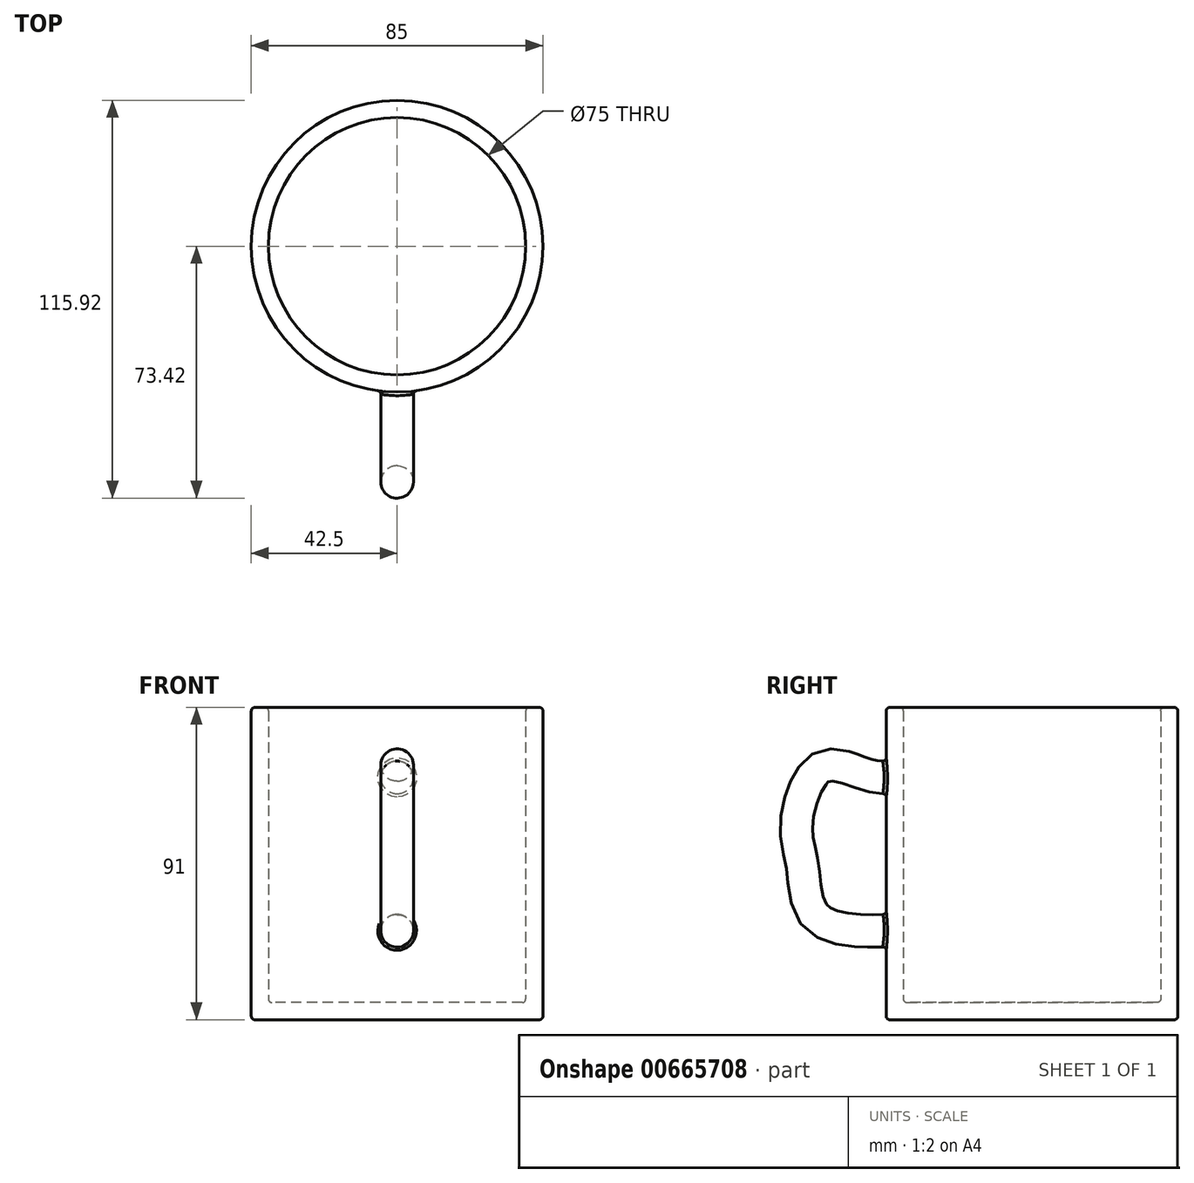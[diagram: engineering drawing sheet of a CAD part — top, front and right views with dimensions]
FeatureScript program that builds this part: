
annotation { "Feature Type Name" : "Feature", "Feature Type Description" : "" }
export const myFeature = defineFeature(function(context is Context, id is Id, definition is map)
    precondition{}
    {
        {
            var Q0;
            Q0=qCreatedBy(makeId("Top.planeOp"),FACE);
            var sketch = newSketch(context, id + "F0", { "sketchPlane" : qUnion([Q0])});
            skCircle(sketch, "E0", {"center": v(0, 0) * mm, "radius": 42.5 * mm});
            skSolve(sketch);
        }
        {
            var Q0;
            Q0 = qSketchRegion(id + "F0", true);
            extrude(context, id + "F1", {"entities" : qUnion([Q0]), "depth" : 91 * mm, "offsetDistance" : 25 * mm});
        }
        {
            var Q0;
            Q0=qCreatedBy(makeId("Right.planeOp"),FACE);
            var sketch = newSketch(context, id + "F2", { "sketchPlane" : qUnion([Q0])});
            skFitSpline(sketch, "E1", {"points": [v(-37.52, 71.63) * mm, v(-47.15, 71.63) * mm, v(-61.16, 74.14) * mm, v(-69.1, 57.41) * mm, v(-67.43, 44.86) * mm, v(-63.25, 29.6) * mm, v(-47.15, 25.4) * mm, v(-38.57, 25.83) * mm], "startDerivative": vector(-74.12, -11.62) * mm, "endDerivative": vector(64.8, 5.7) * mm});
            skSolve(sketch);
        }
        {
            var Q0;
            Q0=qCreatedBy(makeId("Front.planeOp"),FACE);
            cPlane(context, id + "F3", {"entities" : qUnion([Q0]), "cplaneType" : CPlaneType.OFFSET, "offset" : 40 * mm, "width" : 150 * mm, "height" : 150 * mm});
        }
        {
            var Q0;
            Q0=qCreatedBy(id+"F3.planeOp",FACE);
            var sketch = newSketch(context, id + "F4", { "sketchPlane" : qUnion([Q0])});
            skCircle(sketch, "E2", {"center": v(0, 70.8) * mm, "radius": 4.77 * mm});
            skSolve(sketch);
        }
        {
            var Q0;
            Q0 = qSketchRegion(id + "F4", true);
            var Q1;
            Q1=sQuery(id+"F2.wireOp",EDGE,"E1");
            sweep(context, id + "F5", {"operationType" : NewBodyOperationType.ADD, "profiles" : qUnion([Q0]), "path" : qUnion([Q1])});
        }
        {
            var Q0;
            Q0=makeQuery(id+"F1.opExtrude","CAP_FACE",FACE,{"disambiguationData":[OSD([sQuery(id+"F0.wireOp",EDGE,"E0")])],"isStart":false});
            shell(context, id + "F6", {"entities" : qUnion([Q0]), "thickness" : 5 * mm});
        }
        {
            var Q0;
            Q0=makeQuery(id+"F1.opExtrude","CAP_EDGE",EDGE,{"disambiguationData":[OSD([sQuery(id+"F0.wireOp",EDGE,"E0")])],"isStart":true});
            var Q1;
            {var subQ0=sQuery(id+"F0.wireOp",EDGE,"E0");Q1=makeQuery(id+"F6.opShell","OFFSET_EDGE",EDGE,{"disambiguationData":[OSD([subQ0]),TDD([makeQuery(id+"F1.opExtrude","CAP_EDGE",EDGE,{"disambiguationData":[OSD([subQ0])],"isStart":true})])]});}
            var Q2;
            Q2=makeQuery(id+"F1.opExtrude","CAP_FACE",FACE,{"disambiguationData":[OSD([sQuery(id+"F0.wireOp",EDGE,"E0")])],"isStart":false});
            var Q3;
            Q3=makeQuery(id+"F1.opExtrude","CAP_EDGE",EDGE,{"disambiguationData":[OSD([sQuery(id+"F0.wireOp",EDGE,"E0")])],"isStart":false});
            var Q4;
            Q4=makeQuery(id+"F5.boolean.opBoolean","INTERSECT",EDGE,{"disambiguationData":[OD(0.0)],"derivedFrom":[makeQuery(id+"F1.opExtrude","SWEPT_FACE",FACE,{"disambiguationData":[OSD([sQuery(id+"F0.wireOp",EDGE,"E0")])]}),makeQuery(id+"F5.opSweep","SWEPT_FACE",FACE,{"disambiguationData":[OSD([sQuery(id+"F2.wireOp",EDGE,"E1"),sQuery(id+"F4.wireOp",EDGE,"E2")])]})]});
            var Q5;
            Q5=makeQuery(id+"F5.boolean.opBoolean","INTERSECT",EDGE,{"disambiguationData":[OD(1.0)],"derivedFrom":[makeQuery(id+"F1.opExtrude","SWEPT_FACE",FACE,{"disambiguationData":[OSD([sQuery(id+"F0.wireOp",EDGE,"E0")])]}),makeQuery(id+"F5.opSweep","SWEPT_FACE",FACE,{"disambiguationData":[OSD([sQuery(id+"F2.wireOp",EDGE,"E1"),sQuery(id+"F4.wireOp",EDGE,"E2")])]})]});
            fillet(context, id + "F7", {"entities" : qUnion([Q0, Q1, Q2, Q3, Q4, Q5]), "radius" : 1 * mm, "tangentPropagation" : true, "allowEdgeOverflow" : false});
        }
    });
